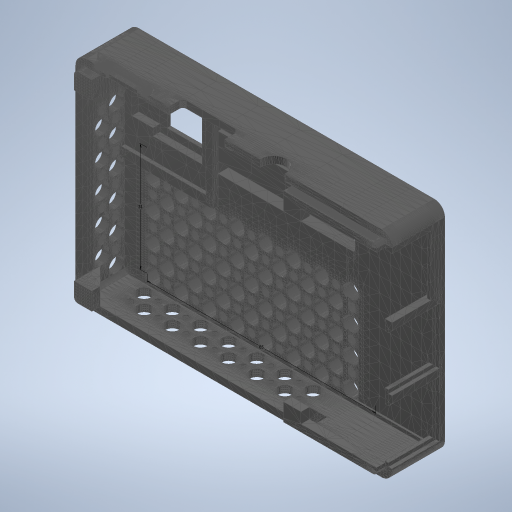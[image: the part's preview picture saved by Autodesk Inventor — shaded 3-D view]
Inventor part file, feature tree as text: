
AUTODESK INVENTOR PART (.ipt)
format: ipt  version: 2023 (Build 270158000, 158)  size: 1,612,800 bytes
history: native  units: mm
features: other x2, sketch x2
ambient origin geometry x8: Origin, YZ Plane, XZ Plane, XY Plane, X Axis, Y Axis, Z Axis, Center Point
feature tree (4):
  other  "top"
  sketch  "Sketch1"  dims[d0=65.0mm]
  sketch  "Sketch2"  dims[d1=31.0mm d2=0.5mm d3=0.872665mm d4=0.5mm d5=0.872665mm]
  other  "MeshFeature1"
